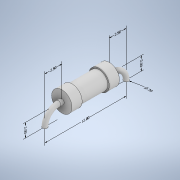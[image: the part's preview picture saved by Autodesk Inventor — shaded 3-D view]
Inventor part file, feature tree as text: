
AUTODESK INVENTOR PART (.ipt)
format: ipt  version: 2021 (Build 250183000, 183)  size: 169,472 bytes
history: native  units: mm
features: other x10, sketch x5, sweep x2, revolve x1
ambient origin geometry x8: Origin, YZ Plane, XZ Plane, XY Plane, X Axis, Y Axis, Z Axis, Center Point
bodies: Body1 (feature_tree)
feature tree (18):
  other  "Таблица"
  other  "Деталь3-01"
  other  "Твердое тело1"
  other  "Аннотации"
  revolve  "Вращение1"
  sketch  "Эскиз2"
  sketch  "Эскиз3"
  sketch  "3D эскиз1"
  sketch  "3D эскиз2"
  sweep  "Сдвиг2"
  sweep  "Сдвиг3"
  sketch  "Эскиз1"
  other  "Линейный размер 1"
  other  "Линейный размер 2"
  other  "Линейный размер 3"
  other  "Линейный размер 4"
  other  "Линейный размер 5"
  other  "Диаметр 1"
